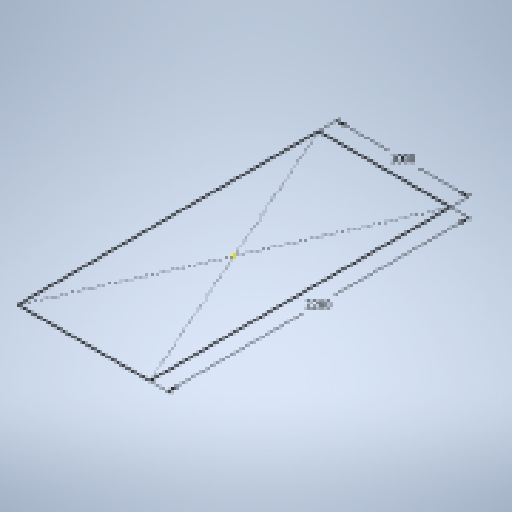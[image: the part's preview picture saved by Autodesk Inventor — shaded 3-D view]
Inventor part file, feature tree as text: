
AUTODESK INVENTOR PART (.ipt)
format: ipt  version: 2025 (Build 290162010, 162A)  size: 167,936 bytes
history: native  units: mm
features: sketch x2, sheet_metal_op x1, extrude x1, pattern_linear x1, other x1, projected_geometry x1
ambient origin geometry x8: Origin, YZ Plane, XZ Plane, XY Plane, X Axis, Y Axis, Z Axis, Center Point
bodies: Solid1 (feature_tree)
feature tree (7):
  sheet_metal_op  "Face1"
  extrude  "Extrusion1"  Depth=2280.0mm
  pattern_linear  "Rectangular Pattern1"  Count1=7  [1 undecoded]
  sketch  "Sketch1"  dims[d0=1000.0mm d1=2280.0mm]
  other  "Plate1"
  sketch  "Sketch2"  dims[d2=10.0mm d3=70.0mm d4=150.5mm d5=0.0mm d6=0.0mm d7=90.0mm d9=250.0mm]
  projected_geometry  "Projected Loop1"
note: 1 required parameter value undecoded (feature->parameter linkage not recoverable at this tier; creation-order binding heuristic only, values carry confidence <= 0.55)
